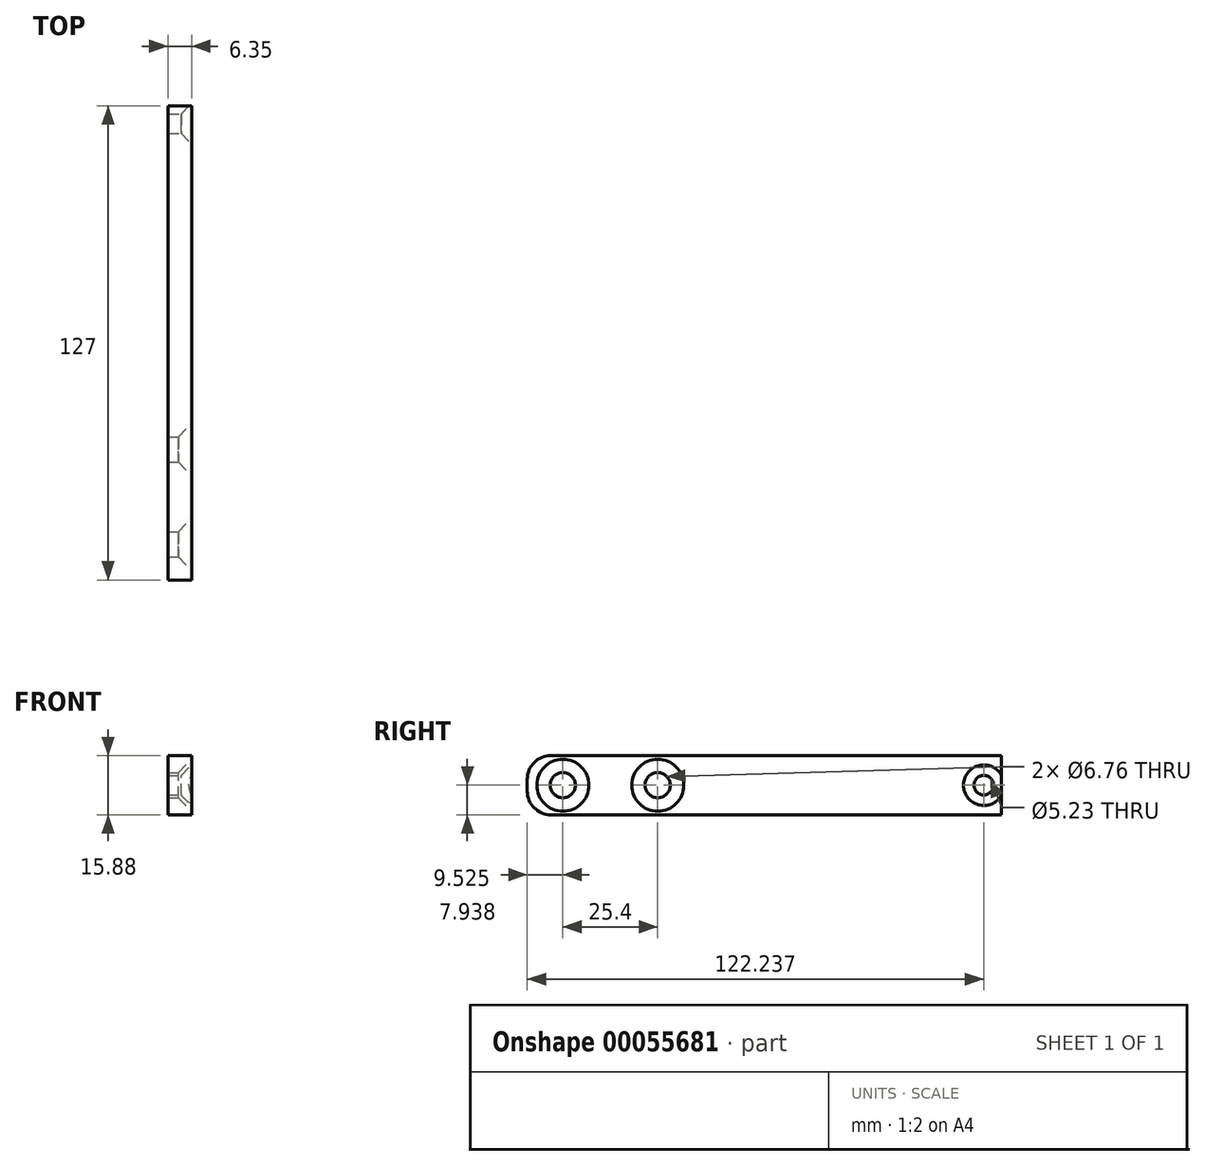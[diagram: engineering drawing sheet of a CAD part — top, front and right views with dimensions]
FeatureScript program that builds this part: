
annotation { "Feature Type Name" : "Feature", "Feature Type Description" : "" }
export const myFeature = defineFeature(function(context is Context, id is Id, definition is map)
    precondition{}
    {
        {
            var Q0;
            Q0=qCreatedBy(makeId("Right.planeOp"),FACE);
            var sketch = newSketch(context, id + "F0", { "sketchPlane" : qUnion([Q0])});
            skLineSegment(sketch, "E0.bottom", {"start": v(0, 0) * mm, "end": v(127, 0) * mm});
            skLineSegment(sketch, "E0.top", {"start": v(0, 15.88) * mm, "end": v(127, 15.88) * mm});
            skLineSegment(sketch, "E0.left", {"start": v(0, 0) * mm, "end": v(0, 15.88) * mm});
            skLineSegment(sketch, "E0.right", {"start": v(127, 0) * mm, "end": v(127, 15.88) * mm});
            skSolve(sketch);
        }
        {
            var Q0;
            Q0 = qSketchRegion(id + "F0", true);
            extrude(context, id + "F1", {"entities" : qUnion([Q0]), "depth" : 6.35 * mm});
        }
        {
            var Q0;
            Q0=makeQuery(id+"F1.opExtrude","CAP_FACE",FACE,{"disambiguationData":[OSD([sQuery(id+"F0.wireOp",EDGE,"E0.bottom"),sQuery(id+"F0.wireOp",EDGE,"E0.top"),sQuery(id+"F0.wireOp",EDGE,"E0.left"),sQuery(id+"F0.wireOp",EDGE,"E0.right")])],"isStart":false});
            var sketch = newSketch(context, id + "F2", { "sketchPlane" : qUnion([Q0])});
            skLineSegment(sketch, "E1", {"start": v(0, 7.94) * mm, "end": v(127, 7.94) * mm});
            skPoint(sketch, "E2", {"position": v(9.53, 7.94) * mm});
            skPoint(sketch, "E3", {"position": v(34.92, 7.94) * mm});
            skPoint(sketch, "E4", {"position": v(122.24, 7.94) * mm});
            skSolve(sketch);
        }
        {
            var Q0;
            Q0=sQuery(id+"F2.wireOp",VERTEX,"E2");
            var Q1;
            Q1=sQuery(id+"F2.wireOp",VERTEX,"E3");
            var Q2;
            Q2=makeQuery(id+"F1.opExtrude","SWEPT_BODY",BODY,{"disambiguationData":[OSD([sQuery(id+"F0.wireOp",EDGE,"E0.bottom"),sQuery(id+"F0.wireOp",EDGE,"E0.top"),sQuery(id+"F0.wireOp",EDGE,"E0.left"),sQuery(id+"F0.wireOp",EDGE,"E0.right")])]});
            hole(context, id + "F3", {"style" : HoleStyle.C_SINK, "holeDiameter" : 6.76 * mm, "cSinkDiameter" : 13.92 * mm, "endStyle" : HoleEndStyle.THROUGH, "locations" : qUnion([Q0, Q1]), "scope" : qUnion([Q2]), "cSinkAngle" : 90 * degree});
        }
        {
            var Q0;
            Q0=sQuery(id+"F2.wireOp",VERTEX,"E4");
            var Q1;
            Q1=makeQuery(id+"F1.opExtrude","SWEPT_BODY",BODY,{"disambiguationData":[OSD([sQuery(id+"F0.wireOp",EDGE,"E0.bottom"),sQuery(id+"F0.wireOp",EDGE,"E0.top"),sQuery(id+"F0.wireOp",EDGE,"E0.left"),sQuery(id+"F0.wireOp",EDGE,"E0.right")])]});
            hole(context, id + "F4", {"style" : HoleStyle.C_SINK, "holeDiameter" : 5.23 * mm, "cSinkDiameter" : 10.87 * mm, "endStyle" : HoleEndStyle.THROUGH, "locations" : qUnion([Q0]), "scope" : qUnion([Q1]), "cSinkAngle" : 90 * degree});
        }
        {
            var Q0;
            Q0=makeQuery(id+"F1.opExtrude","SWEPT_EDGE",EDGE,{"disambiguationData":[OSD([sQuery(id+"F0.wireOp",EDGE,"E0.top"),sQuery(id+"F0.wireOp",EDGE,"E0.left")])]});
            var Q1;
            Q1=makeQuery(id+"F1.opExtrude","SWEPT_EDGE",EDGE,{"disambiguationData":[OSD([sQuery(id+"F0.wireOp",EDGE,"E0.bottom"),sQuery(id+"F0.wireOp",EDGE,"E0.left")])]});
            fillet(context, id + "F5", {"entities" : qUnion([Q0, Q1]), "radius" : 6.35 * mm, "tangentPropagation" : true, "allowEdgeOverflow" : false});
        }
        {
            var Q0;
            Q0=makeQuery(id+"F1.opExtrude","CAP_FACE",FACE,{"disambiguationData":[OSD([sQuery(id+"F0.wireOp",EDGE,"E0.bottom"),sQuery(id+"F0.wireOp",EDGE,"E0.top"),sQuery(id+"F0.wireOp",EDGE,"E0.left"),sQuery(id+"F0.wireOp",EDGE,"E0.right")])],"isStart":true});
            var sketch = newSketch(context, id + "F6", { "sketchPlane" : qUnion([Q0])});
            skLineSegment(sketch, "E5", {"start": v(-122.24, 7.94) * mm, "end": v(-34.92, 7.94) * mm});
            skPoint(sketch, "E6", {"position": v(-70.17, 7.94) * mm});
            skSolve(sketch);
        }
    });
